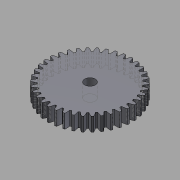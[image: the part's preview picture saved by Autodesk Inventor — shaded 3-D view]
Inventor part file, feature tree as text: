
AUTODESK INVENTOR PART (.ipt)
format: ipt  version: 2015 (Build 190159000, 159)  size: 338,944 bytes
history: native  units: in
note: dims shown in document units (in); Inventor stores cm internally (conversion verified against a paired STEP export)
features: other x13, sketch x3, plane x2
ambient origin geometry x8: Origin, YZ Plane, XZ Plane, XY Plane, X Axis, Y Axis, Z Axis, Center Point
bodies: Solid1 (feature_tree)
feature tree (18):
  other  "Spur Gear2"
  other  "Solid1::Spur Gear2"
  other  "TaggingFeature1"
  sketch  "Sketch1"  dims[d0=0.3937in]
  sketch  "Sketch2"  dims[d16=0.4724in d17=0.0in d41=0.0in d43=0.4724in d46=0.4724in d47=0.0in d48=0.0in]
  sketch  "Sketch3"
  plane  "XZ Plane_1"
  plane  "Work Plane2"
  other  "Z Axis_1"
  other  "Srf1"
  other  "Srf1::Derived"
  other  "Distance iMate"
  other  "Align iMate"
  other  "Mesh iMate"
  other  "Axis iMate"
  other  "Position iMate"
  other  "Mesh iMate2"
  other  "Start plane iMate"
